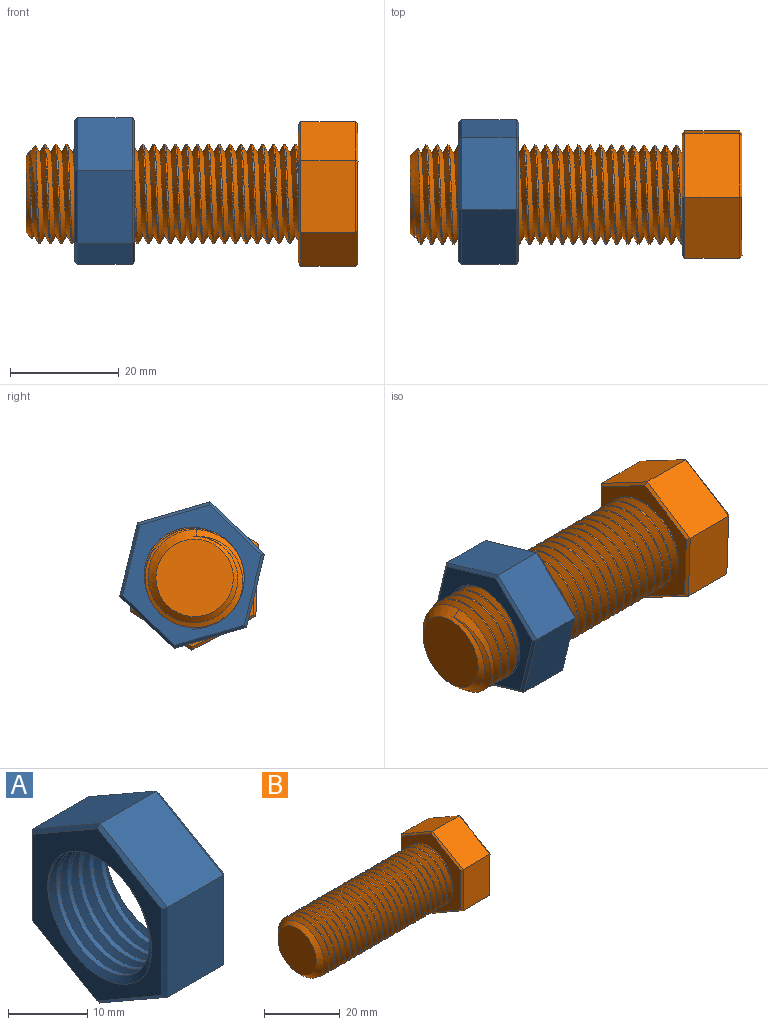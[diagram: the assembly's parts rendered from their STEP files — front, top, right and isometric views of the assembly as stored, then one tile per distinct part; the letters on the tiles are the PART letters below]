
ASSEMBLY  parts=2 mates=1
PART A: 23 faces, bbox 13.3x24.7x28.4 mm
  f0: cylinder r=8.8mm len=17.6mm, axis (1,0,0), area 208.4mm2, adj f7,f8,f21,f22
  f1: plane 11.98x10mm, normal (0,-0.5,0.86), area 138.6mm2, adj f2,f6,f14,f18
  f2: plane 13.86x10mm, normal (0,-1,0), area 138.6mm2, adj f1,f3,f12,f16
  f3: plane 12.02x10mm, normal (0,-0.5,-0.87), area 138.6mm2, adj f2,f4,f10,f15
  f4: plane 11.98x10mm, normal (0,0.5,-0.86), area 138.6mm2, adj f3,f5,f9,f17
  f5: plane 13.86x10mm, normal (0,1,0), area 138.6mm2, adj f4,f6,f11,f19
  f6: plane 12.02x10mm, normal (0,0.5,0.87), area 138.6mm2, adj f1,f5,f13,f20
  f7: plane 27.21x23.69mm, normal (-1,0,0), area 193.9mm2, adj f0,f9,f10,f11,f12,f13,f14,f21
  f8: plane 27.21x23.69mm, normal (1,0,0), area 193.9mm2, adj f0,f15,f16,f17,f18,f19,f20,f21
  f9: plane 11.98x7.25mm, normal (-0.71,0.36,-0.61), area 9.6mm2, adj f4,f7,f10,f11
  f10: plane 12.02x7.19mm, normal (-0.71,-0.35,-0.61), area 9.6mm2, adj f3,f7,f9,f12
  f11: plane 13.86x0.54mm, normal (-0.71,0.71,0), area 9.6mm2, adj f5,f7,f9,f13
  f12: plane 13.86x0.54mm, normal (-0.71,-0.71,0), area 9.6mm2, adj f2,f7,f10,f14
  f13: plane 12.02x7.19mm, normal (-0.71,0.35,0.61), area 9.6mm2, adj f6,f7,f11,f14
  f14: plane 11.98x7.25mm, normal (-0.71,-0.36,0.61), area 9.6mm2, adj f1,f7,f12,f13
  f15: plane 12.02x7.19mm, normal (0.71,-0.35,-0.61), area 9.6mm2, adj f3,f8,f16,f17
  f16: plane 13.86x0.54mm, normal (0.71,-0.71,0), area 9.6mm2, adj f2,f8,f15,f18
  f17: plane 11.98x7.25mm, normal (0.71,0.36,-0.61), area 9.6mm2, adj f4,f8,f15,f19
  f18: plane 11.98x7.25mm, normal (0.71,-0.36,0.61), area 9.6mm2, adj f1,f8,f16,f20
  f19: plane 13.86x0.54mm, normal (0.71,0.71,0), area 9.6mm2, adj f5,f8,f17,f20
  f20: plane 12.02x7.19mm, normal (0.71,0.35,0.61), area 9.6mm2, adj f6,f8,f18,f19
  f21: bspline ~22.92x19.85mm, area 420.1mm2, adj f0,f7,f8,f22
  f22: bspline ~22.92x19.85mm, area 419.8mm2, adj f0,f7,f8,f21
PART B: 26 faces, bbox 61.7x23x26.6 mm
  f0: cylinder r=9.12mm len=48mm, axis (1,0,0), area 77.3mm2, adj f1,f2,f5,f13
  f1: bspline ~50.88x21.06mm, area 2241.6mm2, adj f0,f2,f4,f5,f13
  f2: bspline ~51.88x21.06mm, area -2245.3mm2, adj f0,f1,f4,f5,f13
  f3: plane 14.24x14.24mm, normal (-1,0,0), area 159.3mm2, adj f4
  f4: cone r=9.12mm half-angle=45deg, axis (1,0,0), area 77.6mm2, adj f1,f2,f3,f5
  f5: cone r=9.12mm half-angle=45deg, axis (1,0,0), area 15.8mm2, adj f0,f1,f2,f4
  f6: plane 11.48x10mm, normal (0,-0.5,0.86), area 132.8mm2, adj f7,f11,f19,f23
  f7: plane 13.28x10mm, normal (0,-1,0), area 132.8mm2, adj f6,f8,f17,f21
  f8: plane 11.52x10mm, normal (0,-0.5,-0.87), area 132.8mm2, adj f7,f9,f15,f20
  f9: plane 11.48x10mm, normal (0,0.5,-0.86), area 132.8mm2, adj f8,f10,f14,f22
  f10: plane 13.28x10mm, normal (0,1,0), area 132.8mm2, adj f9,f11,f16,f24
  f11: plane 11.52x10mm, normal (0,0.5,0.87), area 132.8mm2, adj f6,f10,f18,f25
  f12: plane 25.4x22.04mm, normal (1,0,0), area 419.2mm2, adj f14,f15,f16,f17,f18,f19
  f13: plane 25.4x22.04mm, normal (-1,0,0), area 193.7mm2, adj f0,f1,f2,f20,f21,f22,f23,f24
  f14: plane 11.48x6.96mm, normal (0.71,0.36,-0.61), area 9.2mm2, adj f9,f12,f15,f16
  f15: plane 11.52x6.89mm, normal (0.71,-0.35,-0.61), area 9.2mm2, adj f8,f12,f14,f17
  f16: plane 13.28x0.54mm, normal (0.71,0.71,0), area 9.2mm2, adj f10,f12,f14,f18
  f17: plane 13.28x0.54mm, normal (0.71,-0.71,0), area 9.2mm2, adj f7,f12,f15,f19
  f18: plane 11.52x6.89mm, normal (0.71,0.35,0.61), area 9.2mm2, adj f11,f12,f16,f19
  f19: plane 11.48x6.96mm, normal (0.71,-0.36,0.61), area 9.2mm2, adj f6,f12,f17,f18
  f20: plane 11.52x6.89mm, normal (-0.71,-0.35,-0.61), area 9.2mm2, adj f8,f13,f21,f22
  f21: plane 13.28x0.54mm, normal (-0.71,-0.71,0), area 9.2mm2, adj f7,f13,f20,f23
  f22: plane 11.48x6.96mm, normal (-0.71,0.36,-0.61), area 9.2mm2, adj f9,f13,f20,f24
  f23: plane 11.48x6.96mm, normal (-0.71,-0.36,0.61), area 9.2mm2, adj f6,f13,f21,f25
  f24: plane 13.28x0.54mm, normal (-0.71,0.71,0), area 9.2mm2, adj f10,f13,f22,f25
  f25: plane 11.52x6.89mm, normal (-0.71,0.35,0.61), area 9.2mm2, adj f11,f13,f23,f24
PLACE A rot(axis=(0,0.6,-0.8),180deg) t=(-55.27,-6.86,23.48)mm
PLACE B rot(axis=(-1,0,0),178.1deg) t=(-8.77,-7.34,22.97)mm
MATE cylindrical B.f0 <-> A.f7  axis (-1,0,0) through (-64.27,-7.34,22.97)mm
